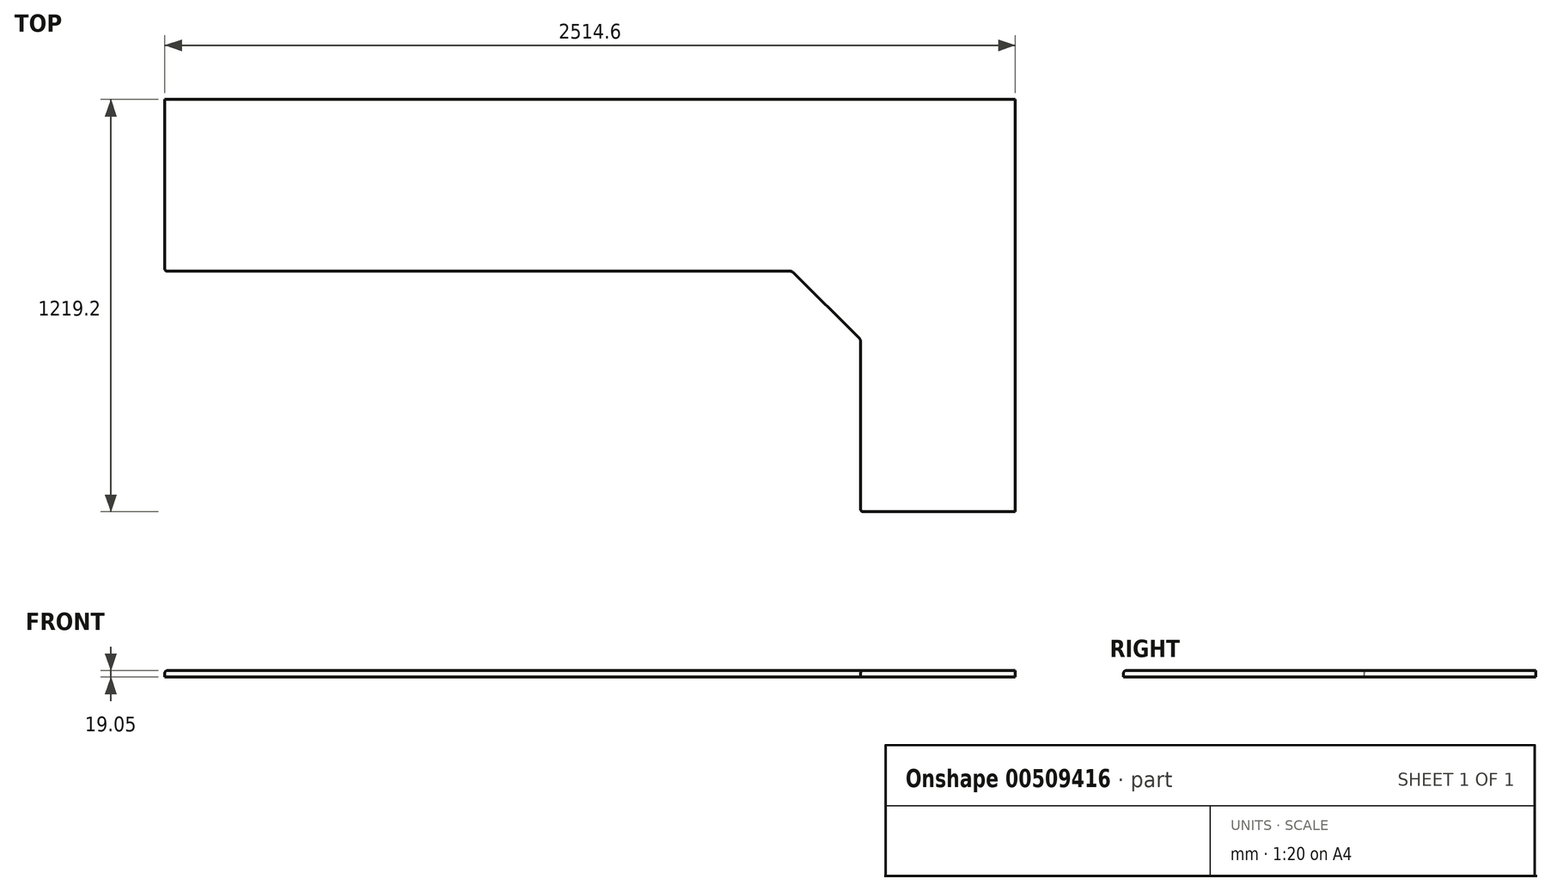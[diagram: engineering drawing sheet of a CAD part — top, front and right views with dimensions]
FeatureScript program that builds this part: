
annotation { "Feature Type Name" : "Feature", "Feature Type Description" : "" }
export const myFeature = defineFeature(function(context is Context, id is Id, definition is map)
    precondition{}
    {
        {
            var Q0;
            Q0=qCreatedBy(makeId("Top.planeOp"),FACE);
            var sketch = newSketch(context, id + "F0", { "sketchPlane" : qUnion([Q0])});
            skLineSegment(sketch, "E0", {"start": v(0, 0) * mm, "end": v(-2514.6, 0) * mm});
            skLineSegment(sketch, "E1", {"start": v(-2514.6, 0) * mm, "end": v(-2514.6, -508) * mm});
            skLineSegment(sketch, "E2", {"start": v(-2514.6, -508) * mm, "end": v(-660.4, -508) * mm});
            skLineSegment(sketch, "E3", {"start": v(-660.4, -508) * mm, "end": v(-457.2, -711.2) * mm});
            skLineSegment(sketch, "E4", {"start": v(-457.2, -711.2) * mm, "end": v(-457.2, -1219.2) * mm});
            skLineSegment(sketch, "E5", {"start": v(-457.2, -1219.2) * mm, "end": v(0, -1219.2) * mm});
            skLineSegment(sketch, "E6", {"start": v(0, -1219.2) * mm, "end": v(0, 0) * mm});
            skSolve(sketch);
        }
        {
            var Q0;
            Q0 = qSketchRegion(id + "F0", true);
            extrude(context, id + "F1", {"entities" : qUnion([Q0]), "depth" : 19.05 * mm});
        }
        {
            var Q0;
            Q0=makeQuery(id+"F1.opExtrude","SWEPT_EDGE",EDGE,{"disambiguationData":[OSD([sQuery(id+"F0.wireOp",EDGE,"E2"),sQuery(id+"F0.wireOp",EDGE,"E3")])]});
            var Q1;
            Q1=makeQuery(id+"F1.opExtrude","SWEPT_EDGE",EDGE,{"disambiguationData":[OSD([sQuery(id+"F0.wireOp",EDGE,"E3"),sQuery(id+"F0.wireOp",EDGE,"E4")])]});
            fillet(context, id + "F2", {"entities" : qUnion([Q0, Q1]), "radius" : 12.7 * mm, "tangentPropagation" : true, "allowEdgeOverflow" : false});
        }
        {
            var Q0;
            Q0=makeQuery(id+"F1.opExtrude","CAP_EDGE",EDGE,{"disambiguationData":[OSD([sQuery(id+"F0.wireOp",EDGE,"E2")])],"isStart":false});
            fillet(context, id + "F3", {"entities" : qUnion([Q0]), "radius" : 6.35 * mm, "tangentPropagation" : true, "allowEdgeOverflow" : false});
        }
        {
            var Q0;
            Q0=makeQuery(id+"F1.opExtrude","CAP_EDGE",EDGE,{"disambiguationData":[OSD([sQuery(id+"F0.wireOp",EDGE,"E5")])],"isStart":false});
            var Q1;
            Q1=makeQuery(id+"F1.opExtrude","CAP_EDGE",EDGE,{"disambiguationData":[OSD([sQuery(id+"F0.wireOp",EDGE,"E1")])],"isStart":false});
            fillet(context, id + "F4", {"entities" : qUnion([Q0, Q1]), "radius" : 6.35 * mm, "tangentPropagation" : true, "allowEdgeOverflow" : false});
        }
    });
